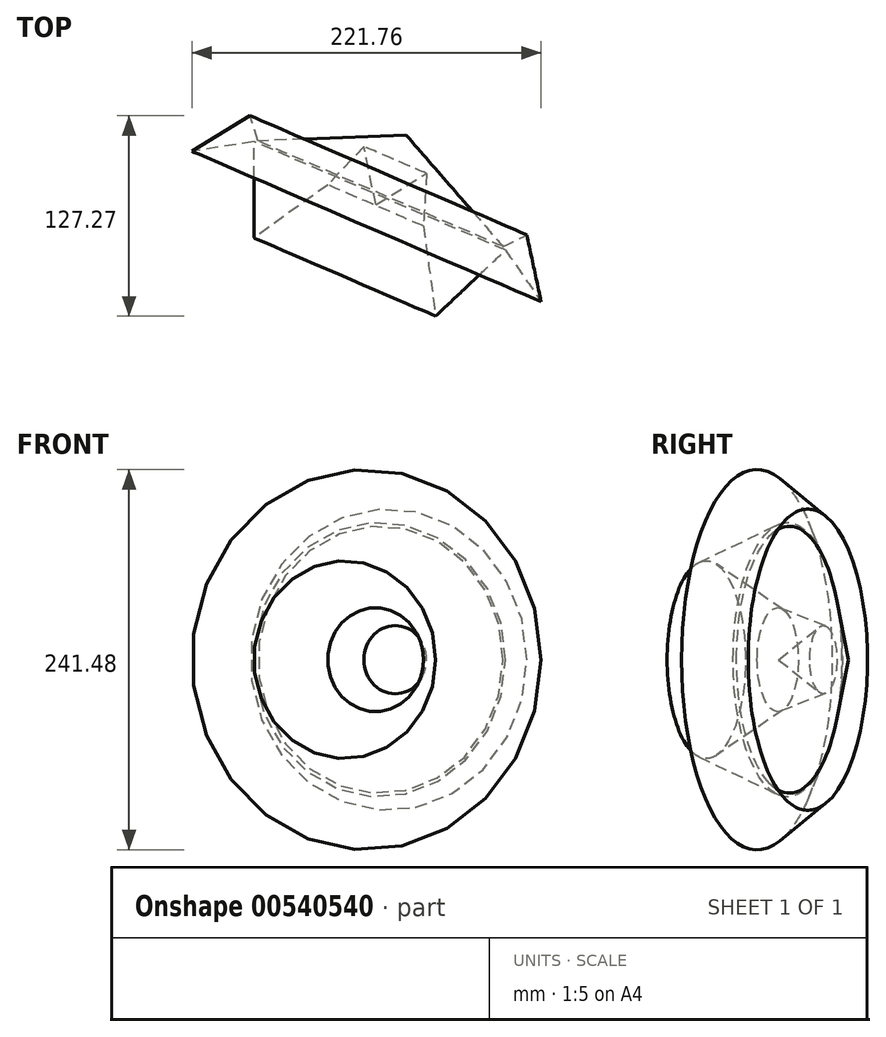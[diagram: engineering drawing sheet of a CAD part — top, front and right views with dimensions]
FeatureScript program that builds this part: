
annotation { "Feature Type Name" : "Feature", "Feature Type Description" : "" }
export const myFeature = defineFeature(function(context is Context, id is Id, definition is map)
    precondition{}
    {
        {
            var Q0;
            Q0=qCreatedBy(makeId("Top.planeOp"),FACE);
            var sketch = newSketch(context, id + "F0", { "sketchPlane" : qUnion([Q0])});
            skLineSegment(sketch, "E0", {"start": v(-30.93, 44.86) * mm, "end": v(-30.93, -16.23) * mm});
            skLineSegment(sketch, "E1", {"start": v(-30.93, -16.23) * mm, "end": v(16.04, 17.37) * mm});
            skLineSegment(sketch, "E2", {"start": v(16.04, 17.37) * mm, "end": v(38.94, 41.8) * mm});
            skLineSegment(sketch, "E3", {"start": v(38.94, 41.8) * mm, "end": v(46.58, 4.77) * mm});
            skLineSegment(sketch, "E4", {"start": v(46.58, 4.77) * mm, "end": v(65.67, 49.06) * mm});
            skLineSegment(sketch, "E5", {"start": v(65.67, 49.06) * mm, "end": v(-28.25, 45.24) * mm});
            skLineSegment(sketch, "E6", {"start": v(-28.25, 45.24) * mm, "end": v(-33.22, 61.28) * mm});
            skLineSegment(sketch, "E7", {"start": v(-33.22, 61.28) * mm, "end": v(-70.25, 38.75) * mm});
            skLineSegment(sketch, "E8", {"start": v(-70.25, 38.75) * mm, "end": v(-30.93, 44.86) * mm});
            skSolve(sketch);
        }
        {
            var Q0;
            Q0=makeQuery(id+"F0.imprint","IMPRINT",FACE,{"disambiguationData":[TD([[makeQuery(id+"F0.imprint","IMPRINT",EDGE,{"derivedFrom":sQuery(id+"F0.wireOp",EDGE,"E0")}),1.0]])]});
            var Q1;
            Q1=sQuery(id+"F0.wireOp",EDGE,"E4");
            revolve(context, id + "F1", {"entities" : qUnion([Q0]), "axis" : qUnion([Q1]), "revolveType" : RevolveType.FULL});
        }
    });
